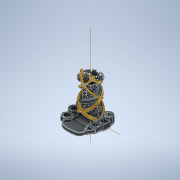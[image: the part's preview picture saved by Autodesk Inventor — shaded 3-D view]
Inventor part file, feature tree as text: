
AUTODESK INVENTOR PART (.ipt)
format: ipt  version: 2022 (Build 260153000, 153)  size: 7,655,424 bytes
history: native  units: mm
features: sketch x26, extrude x25, helix x5, plane x4, fillet x3, revolve x2, pattern_circular x2, chamfer x2
ambient origin geometry x8: Origin, YZ Plane, XZ Plane, XY Plane, X Axis, Y Axis, Z Axis, Center Point
bodies: Solid1 (feature_tree)
feature tree (69):
  revolve  "Revolution1"  [1 undecoded]
  plane  "Work Plane1"
  extrude  "Extrusion4"  Depth=20.0mm
  extrude  "Extrusion2"  Depth=19.0mm
  pattern_circular  "Circular Pattern2"  Count=9  [1 undecoded]
  plane  "Work Plane3"
  extrude  "Extrusion3"  Depth=10.0mm
  pattern_circular  "Circular Pattern3"  Count=7  [1 undecoded]
  helix  "Coil1"  [1 undecoded]
  helix  "Coil2"  [1 undecoded]
  helix  "Coil3"  [1 undecoded]
  helix  "Coil4"  [1 undecoded]
  helix  "Coil5"  [1 undecoded]
  extrude  "Extrusion5"  Depth=20.0mm
  revolve  "Revolution2"  [1 undecoded]
  extrude  "Extrusion6"  Depth=30.0mm
  extrude  "Extrusion15"  Depth=15.0mm
  extrude  "Extrusion16"  Depth=30.0mm
  extrude  "Extrusion17"  Depth=45.0mm
  extrude  "Extrusion18"  Depth=13.0mm
  extrude  "Extrusion19"  Depth=39.0mm
  extrude  "Extrusion20"  Depth=11.0mm
  extrude  "Extrusion21"  Depth=10.0mm
  extrude  "Extrusion22"  Depth=11.0mm
  extrude  "Extrusion23"  Depth=9.0mm
  extrude  "Extrusion25"  Depth=3.0mm TaperAngle=0.0deg
  extrude  "Extrusion26"  Depth=54.0mm TaperAngle=0.0deg
  extrude  "Extrusion27"  Depth=35.0mm
  extrude  "Extrusion28"  Depth=35.0mm
  extrude  "Extrusion29"  Depth=30.0mm
  extrude  "Extrusion30"  Depth=30.0mm
  extrude  "Extrusion31"  Depth=35.0mm
  plane  "Work Plane4"
  extrude  "Extrusion32"  Depth=35.0mm
  extrude  "Extrusion33"  Depth=5.0mm
  chamfer  "Chamfer2"  Distance=10.0mm
  chamfer  "Chamfer3"  Distance=5.0mm
  fillet  "Fillet5"  Radius=10.0mm
  fillet  "Fillet6"  Radius=15.0mm
  extrude  "Extrusion34"  Depth=0.2mm TaperAngle=0.0deg
  fillet  "Fillet16"  Radius=5.0mm
  extrude  "Extrusion35"  Depth=10.0mm TaperAngle=0.0deg
  sketch  "Sketch1"  dims[d11=50.0mm d12=40.0mm]
  sketch  "Sketch3"  dims[d13=20.0mm d14=20.0mm]
  plane  "Work Plane2"
  sketch  "Sketch4"  dims[d15=23.0mm d16=19.0mm d17=90.0mm]
  sketch  "Sketch5"  dims[d18=32.0mm d19=10.0mm]
  sketch  "Sketch7"  dims[d20=151.0mm]
  sketch  "Sketch8"  dims[d26=2.0mm]
  sketch  "Sketch9"  dims[d27=2.0mm]
  sketch  "Sketch10"  dims[d28=2.0mm]
  sketch  "Sketch11"  dims[d29=2.0mm]
  sketch  "Sketch13"  dims[d30=2.0mm]
  sketch  "Sketch16"  dims[d31=90.0deg d32=70.0mm d38=77.75mm d39=0.0mm d40=40.0mm d41=360.0deg d43=70.0mm d44=77.75mm d45=0.0mm d46=40.0mm d47=360.0deg]
  sketch  "Sketch17"  dims[d49=20.0mm d50=20.0mm]
  sketch  "Sketch20"  dims[d51=20.0mm d52=20.0mm]
  sketch  "Sketch21"  dims[d53=40.0mm d54=30.0mm]
  sketch  "Sketch22"  dims[d55=30.0mm d56=15.0mm]
  sketch  "Sketch26"  dims[d57=15.0mm d58=30.0mm]
  sketch  "Sketch27"  dims[d59=77.75mm d60=0.0mm d61=45.0mm]
  sketch  "Sketch28"  dims[d62=35.0mm]
  sketch  "Sketch30"  dims[d63=70.0mm d64=100.0mm d65=10.0mm d66=-0.567232mm d67=90.0deg d68=90.0deg d69=90.0deg d70=90.0deg d71=13.0mm]
  sketch  "Sketch31"  dims[d72=10.0mm d73=39.0mm]
  sketch  "Sketch33"  dims[d74=140.0mm d75=160.0mm d76=10.0mm d77=-0.645772mm d78=90.0deg d79=90.0deg d80=90.0deg d81=90.0deg d82=11.0mm]
  sketch  "Sketch35"  dims[d83=39.0mm d84=10.0mm]
  sketch  "Sketch37"  dims[d85=135.0mm d86=160.0mm d87=10.0mm d88=-0.645772mm d89=90.0deg d90=90.0deg d91=90.0deg d92=90.0deg d93=11.0mm]
  sketch  "Sketch41"  dims[d94=170.0mm d95=160.0mm d96=10.0mm d97=-0.645772mm d98=90.0deg d99=90.0deg d100=90.0deg d101=90.0deg d102=9.0mm]
  sketch  "Sketch43"  dims[d103=170.0mm d104=160.0mm d105=10.0mm d106=-0.645772mm d107=90.0deg d108=90.0deg d109=90.0deg d110=90.0deg d125=3.0mm d126=0.0mm]
  sketch  "Sketch44"  dims[d130=270.0deg d133=54.0mm d134=0.0mm d141=35.0mm d165=35.0mm d166=30.0mm d167=30.0mm d168=30.0mm d169=30.0mm d170=35.0mm d172=35.0mm d186=5.0mm d187=10.0mm d188=0.0mm d190=5.0mm d191=0.0mm d192=10.0mm d193=0.0mm d194=15.0mm d195=0.0mm d196=0.2mm d197=0.0mm d198=5.0mm d199=0.0mm d200=10.0mm d201=0.0mm d202=15.0mm d203=0.0mm d204=3.0mm d205=0.0mm d210=1.0mm d211=0.0mm d213=10.0mm d214=0.0mm d218=30.0mm d219=23.5mm d220=5.75mm d221=5.75mm d222=5.75mm d223=14.0mm d224=0.0mm d225=22.5mm d226=6.25mm d227=6.25mm d228=6.25mm d229=14.0mm d230=0.0mm d235=14.0mm d236=0.0mm d241=10.0mm d242=0.0mm d245=17.5mm d251=10.0mm d252=0.0mm d254=21.0mm d258=24.0mm d259=0.0mm d263=25.0mm d266=5.0mm d267=5.0mm d268=12.0mm d269=0.0mm d270=11.0mm d271=2.0mm d272=45.0deg d273=12.0mm d274=2.0mm d275=45.0deg d276=35.0mm d278=5.0mm d279=5.0mm d280=5.0mm d282=2.0mm d283=1.0mm d292=20.0mm d293=0.0mm d295=2.0mm d299=25.0mm d300=52.0mm d301=54.0mm d302=0.0mm d303=25.0mm d304=5.0mm d305=5.0mm d306=5.0mm d307=5.0mm d308=26.0mm d309=3.0mm d310=2.0mm d311=2.484774mm d312=17.5mm d313=21.0mm d132=0.0mm d135=0.0mm]
note: 9 required parameter values undecoded (feature->parameter linkage not recoverable at this tier; creation-order binding heuristic only, values carry confidence <= 0.55)